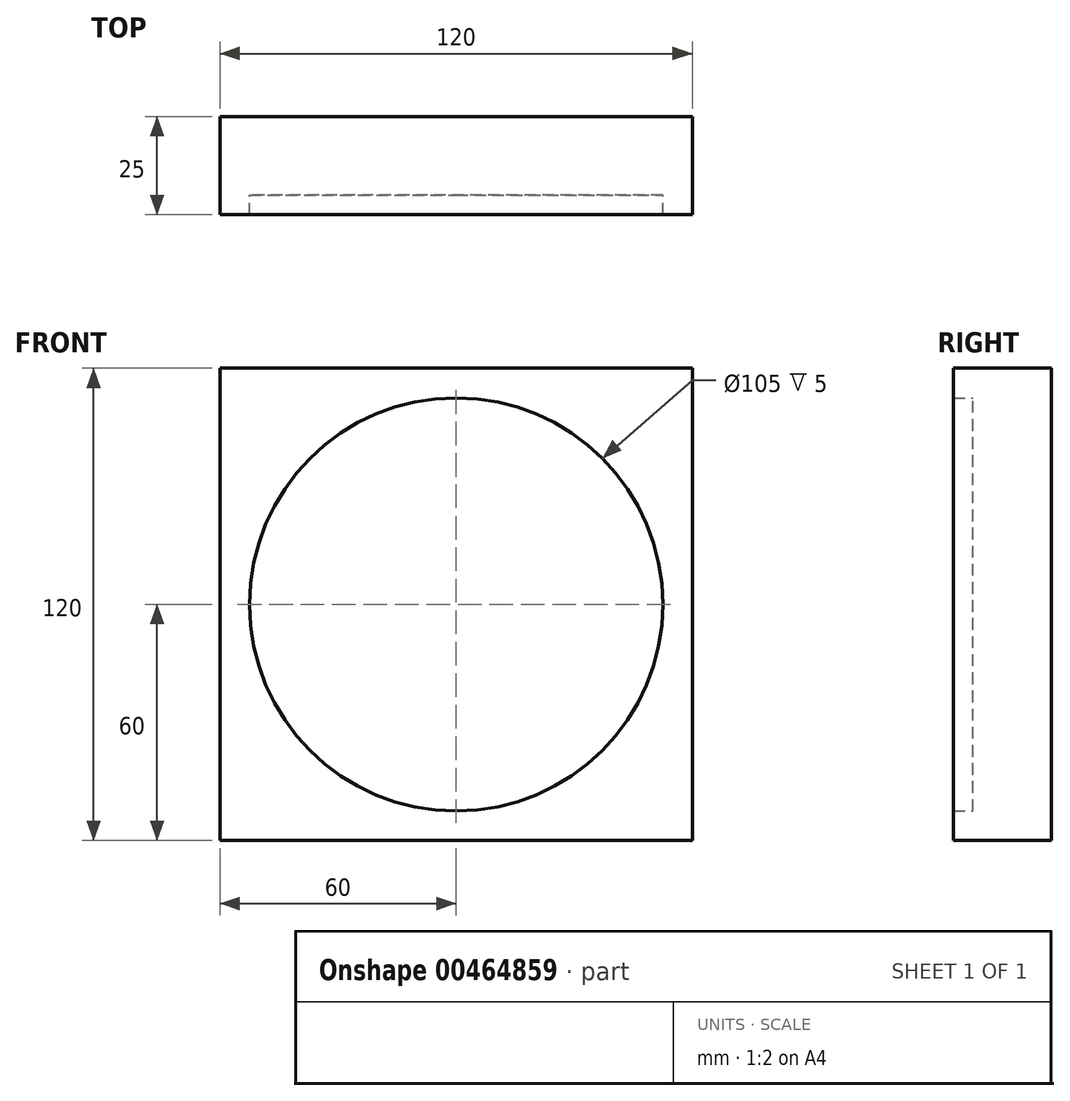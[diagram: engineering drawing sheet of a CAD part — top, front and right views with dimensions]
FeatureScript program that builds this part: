
annotation { "Feature Type Name" : "Feature", "Feature Type Description" : "" }
export const myFeature = defineFeature(function(context is Context, id is Id, definition is map)
    precondition{}
    {
        {
            var Q0;
            Q0=qCreatedBy(makeId("Front.planeOp"),FACE);
            var sketch = newSketch(context, id + "F0", { "sketchPlane" : qUnion([Q0])});
            skLineSegment(sketch, "E0.bottom", {"start": v(-60, 60) * mm, "end": v(60, 60) * mm});
            skLineSegment(sketch, "E0.top", {"start": v(-60, -60) * mm, "end": v(60, -60) * mm});
            skLineSegment(sketch, "E0.left", {"start": v(-60, 60) * mm, "end": v(-60, -60) * mm});
            skLineSegment(sketch, "E0.right", {"start": v(60, 60) * mm, "end": v(60, -60) * mm});
            skPoint(sketch, "E0.middle", {"position": v(0, 0) * mm});
            skCircle(sketch, "E1", {"center": v(0, 0) * mm, "radius": 52.5 * mm});
            skSolve(sketch);
        }
        {
            var Q0;
            Q0=makeQuery(id+"F0.imprint","IMPRINT",FACE,{"disambiguationData":[TD([[makeQuery(id+"F0.imprint","IMPRINT",EDGE,{"derivedFrom":sQuery(id+"F0.wireOp",EDGE,"E0.bottom")}),-1.0]])]});
            extrude(context, id + "F1", {"entities" : qUnion([Q0]), "depth" : 25 * mm});
        }
        {
            var Q0;
            Q0=makeQuery(id+"F0.imprint","IMPRINT",FACE,{"disambiguationData":[TD([[makeQuery(id+"F0.imprint","IMPRINT",EDGE,{"derivedFrom":sQuery(id+"F0.wireOp",EDGE,"E1")}),1.0]])]});
            extrude(context, id + "F2", {"entities" : qUnion([Q0]), "operationType" : NewBodyOperationType.ADD, "depth" : 20 * mm});
        }
    });
